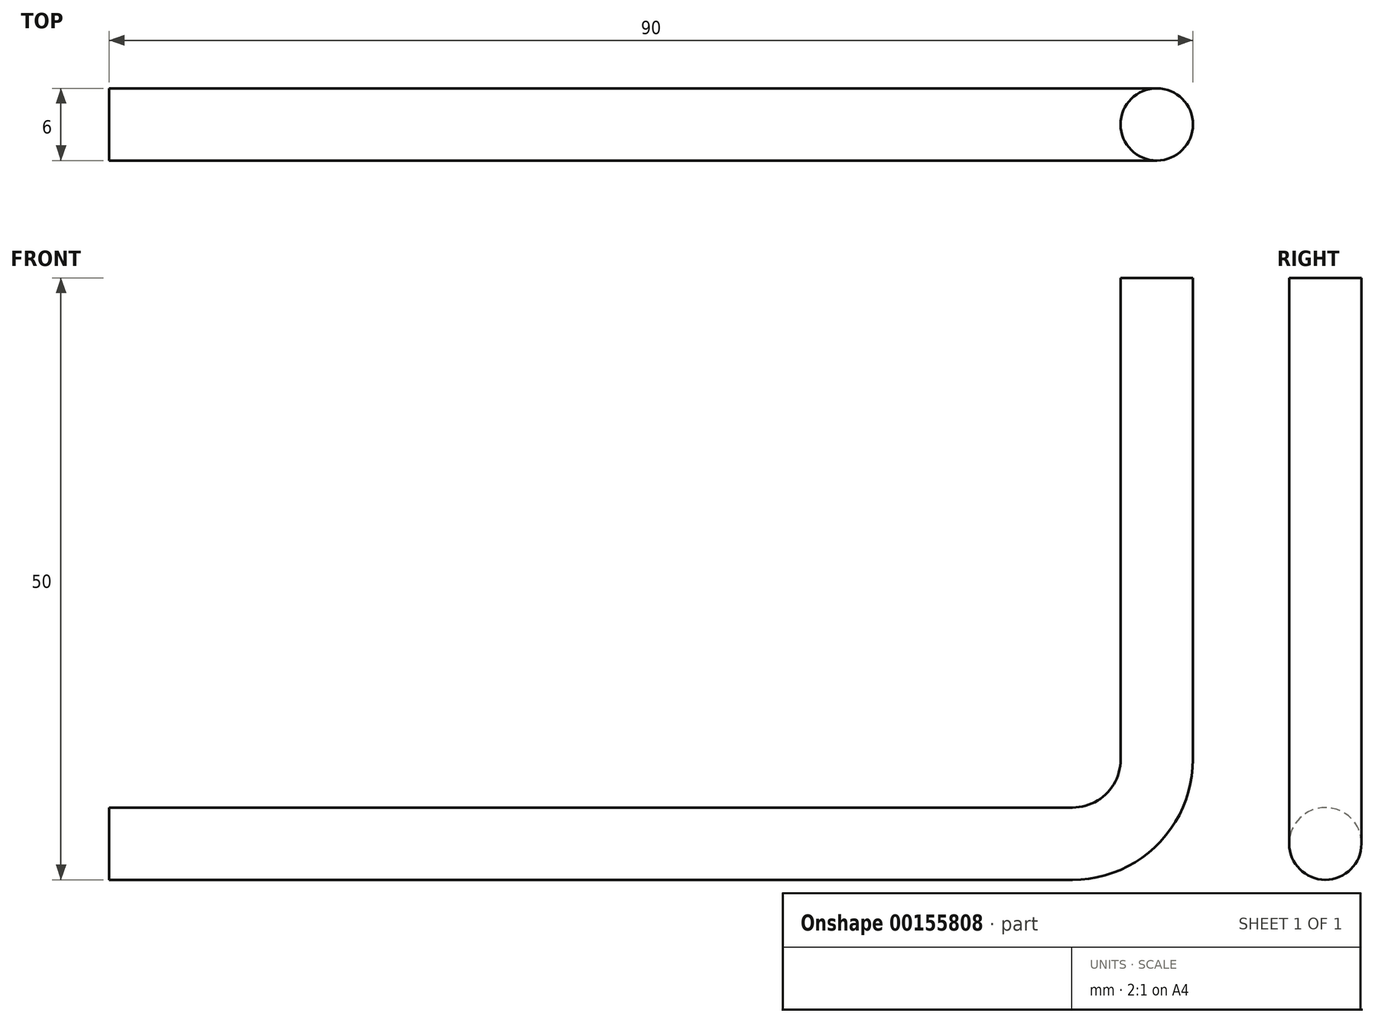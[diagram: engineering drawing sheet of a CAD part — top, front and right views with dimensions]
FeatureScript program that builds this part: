
annotation { "Feature Type Name" : "Feature", "Feature Type Description" : "" }
export const myFeature = defineFeature(function(context is Context, id is Id, definition is map)
    precondition{}
    {
        {
            var Q0;
            Q0=qCreatedBy(makeId("Front.planeOp"),FACE);
            var sketch = newSketch(context, id + "F0", { "sketchPlane" : qUnion([Q0])});
            skLineSegment(sketch, "E0", {"start": v(0, 0) * mm, "end": v(80, 0) * mm});
            skArc(sketch, "E1", {"start": v(80, 0) * mm, "mid": v(84.95, 2.05) * mm, "end": v(87, 7) * mm});
            skLineSegment(sketch, "E2", {"start": v(87, 7) * mm, "end": v(87, 47) * mm});
            skSolve(sketch);
        }
        {
            var Q0;
            Q0=qCreatedBy(makeId("Right.planeOp"),FACE);
            var sketch = newSketch(context, id + "F1", { "sketchPlane" : qUnion([Q0])});
            skCircle(sketch, "E3", {"center": v(0, 0) * mm, "radius": 3 * mm});
            skSolve(sketch);
        }
        {
            var Q0;
            Q0=makeQuery(id+"F1.imprint","IMPRINT",FACE,{"disambiguationData":[TD([[makeQuery(id+"F1.imprint","IMPRINT",EDGE,{"derivedFrom":sQuery(id+"F1.wireOp",EDGE,"E3")}),1.0]])]});
            var Q1;
            Q1=sQuery(id+"F0.wireOp",EDGE,"ev8xvnma-Kx5n-LJW8-0ofH-jus9e5lSajr3");
            var Q2;
            Q2=sQuery(id+"F0.wireOp",EDGE,"E0");
            var Q3;
            Q3=sQuery(id+"F0.wireOp",EDGE,"E1");
            var Q4;
            Q4=sQuery(id+"F0.wireOp",EDGE,"E2");
            var Q5;
            Q5=sQuery(id+"F0.wireOp",EDGE,"2TiX2ViZ-t8sK-9hUQ-MlfC-gPFm1rc3iv9g");
            sweep(context, id + "F2", {"profiles" : qUnion([Q0]), "path" : qUnion([Q1, Q2, Q3, Q4, Q5])});
        }
    });
